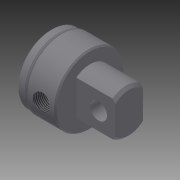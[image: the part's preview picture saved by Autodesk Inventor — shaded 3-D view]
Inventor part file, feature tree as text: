
AUTODESK INVENTOR PART (.ipt)
format: ipt  version: 2014 (Build 180170000, 170)  size: 261,632 bytes
history: native  units: in
note: dims shown in document units (in); Inventor stores cm internally (conversion verified against a paired STEP export)
features: other x126, sketch x8, revolve x5, extrude x2, hole x1, thread x1
ambient origin geometry x8: Origin, YZ Plane, XZ Plane, XY Plane, X Axis, Y Axis, Z Axis, Center Point
bodies: Solid1 (feature_tree)
feature tree (143):
  revolve  "Revolution1"  Angle=360.0deg
  revolve  "Revolution2"  Angle=360.0deg
  extrude  "Extrusion1"  TaperAngle=360.0deg  [1 undecoded]
  hole  "Hole1"  [1 undecoded]
  revolve  "Revolution3"  [1 undecoded]
  thread  "Thread1"  [1 undecoded]
  revolve  "Revolution4"  [1 undecoded]
  revolve  "Revolution5"  [1 undecoded]
  extrude  "Extrusion2"  [1 undecoded]
  other  "f_XY"
  other  "f_YZ"
  other  "f_ZX"
  other  "f_X"
  other  "f_Y"
  other  "f_Z"
  other  "f_Center"
  other  "lovra1_XY"
  other  "lovra1_YZ"
  other  "lovra1_ZX"
  other  "lovra1_X"
  other  "lovra1_Y"
  other  "lovra1_Z"
  other  "lovra1_Center"
  other  "lovra2_XY"
  other  "lovra2_YZ"
  other  "lovra2_ZX"
  other  "lovra2_X"
  other  "lovra2_Y"
  other  "lovra2_Z"
  other  "lovra2_Center"
  other  "lovra21_XY"
  other  "lovra21_YZ"
  other  "lovra21_ZX"
  other  "lovra21_X"
  other  "lovra21_Y"
  other  "lovra21_Z"
  other  "lovra21_Center"
  other  "lovra22_XY"
  other  "lovra22_YZ"
  other  "lovra22_ZX"
  other  "lovra22_X"
  other  "lovra22_Y"
  other  "lovra22_Z"
  other  "lovra22_Center"
  other  "lovra3_XY"
  other  "lovra3_YZ"
  other  "lovra3_ZX"
  other  "lovra3_X"
  other  "lovra3_Y"
  other  "lovra3_Z"
  other  "lovra3_Center"
  other  "olen_XY"
  other  "olen_YZ"
  other  "olen_ZX"
  other  "olen_X"
  other  "olen_Y"
  other  "olen_Z"
  other  "olen_Center"
  other  "p1_XY"
  other  "p1_YZ"
  other  "p1_ZX"
  other  "p1_X"
  other  "p1_Y"
  other  "p1_Z"
  other  "p1_Center"
  other  "p2_XY"
  other  "p2_YZ"
  other  "p2_ZX"
  other  "p2_X"
  other  "p2_Y"
  other  "p2_Z"
  other  "p2_Center"
  other  "port_XY"
  other  "port_YZ"
  other  "port_ZX"
  other  "port_X"
  other  "port_Y"
  other  "port_Z"
  other  "port_Center"
  other  "port2_XY"
  other  "port2_YZ"
  other  "port2_ZX"
  other  "port2_X"
  other  "port2_Y"
  other  "port2_Z"
  other  "port2_Center"
  other  "thd1_XY"
  other  "thd1_YZ"
  other  "thd1_ZX"
  other  "thd1_X"
  other  "thd1_Y"
  other  "thd1_Z"
  other  "thd1_Center"
  other  "thd2_XY"
  other  "thd2_YZ"
  other  "thd2_ZX"
  other  "thd2_X"
  other  "thd2_Y"
  other  "thd2_Z"
  other  "thd2_Center"
  other  "to_mounting_bracket_XY"
  other  "to_mounting_bracket_YZ"
  other  "to_mounting_bracket_ZX"
  other  "to_mounting_bracket_X"
  other  "to_mounting_bracket_Y"
  other  "to_mounting_bracket_Z"
  other  "to_mounting_bracket_Center"
  other  "to_nut_XY"
  other  "to_nut_YZ"
  other  "to_nut_ZX"
  other  "to_nut_X"
  other  "to_nut_Y"
  other  "to_nut_Z"
  other  "to_nut_Center"
  other  "to_pin_XY"
  other  "to_pin_YZ"
  other  "to_pin_ZX"
  other  "to_pin_X"
  other  "to_pin_Y"
  other  "to_pin_Z"
  other  "to_pin_Center"
  other  "to_screw_XY"
  other  "to_screw_YZ"
  other  "to_screw_ZX"
  other  "to_screw_X"
  other  "to_screw_Y"
  other  "to_screw_Z"
  other  "to_screw_Center"
  other  "to_tube_XY"
  other  "to_tube_YZ"
  other  "to_tube_ZX"
  other  "to_tube_X"
  other  "to_tube_Y"
  other  "to_tube_Z"
  other  "to_tube_Center"
  sketch  "Sketch_18"  dims[d4=0.532in d5=0.75in d6=0.375in d7=0.25in d8=0.5635in d9=0.8052in d10=120.0deg d11=360.0deg]
  sketch  "Sketch_21"  dims[d15=360.0deg d16=0.9255in d17=0.0in]
  sketch  "Sketch_9"  dims[d2=0.875in d3=0.0in]
  sketch  "Sketch4"  dims[d0=360.0deg d1=360.0deg]
  sketch  "Sketch_68"
  sketch  "Sketch_20"  dims[d12=0.2731in d13=0.0in d14=360.0deg]
  sketch  "Sketch_24"
  sketch  "Sketch_43"
note: 7 required parameter values undecoded (feature->parameter linkage not recoverable at this tier; creation-order binding heuristic only, values carry confidence <= 0.55)
